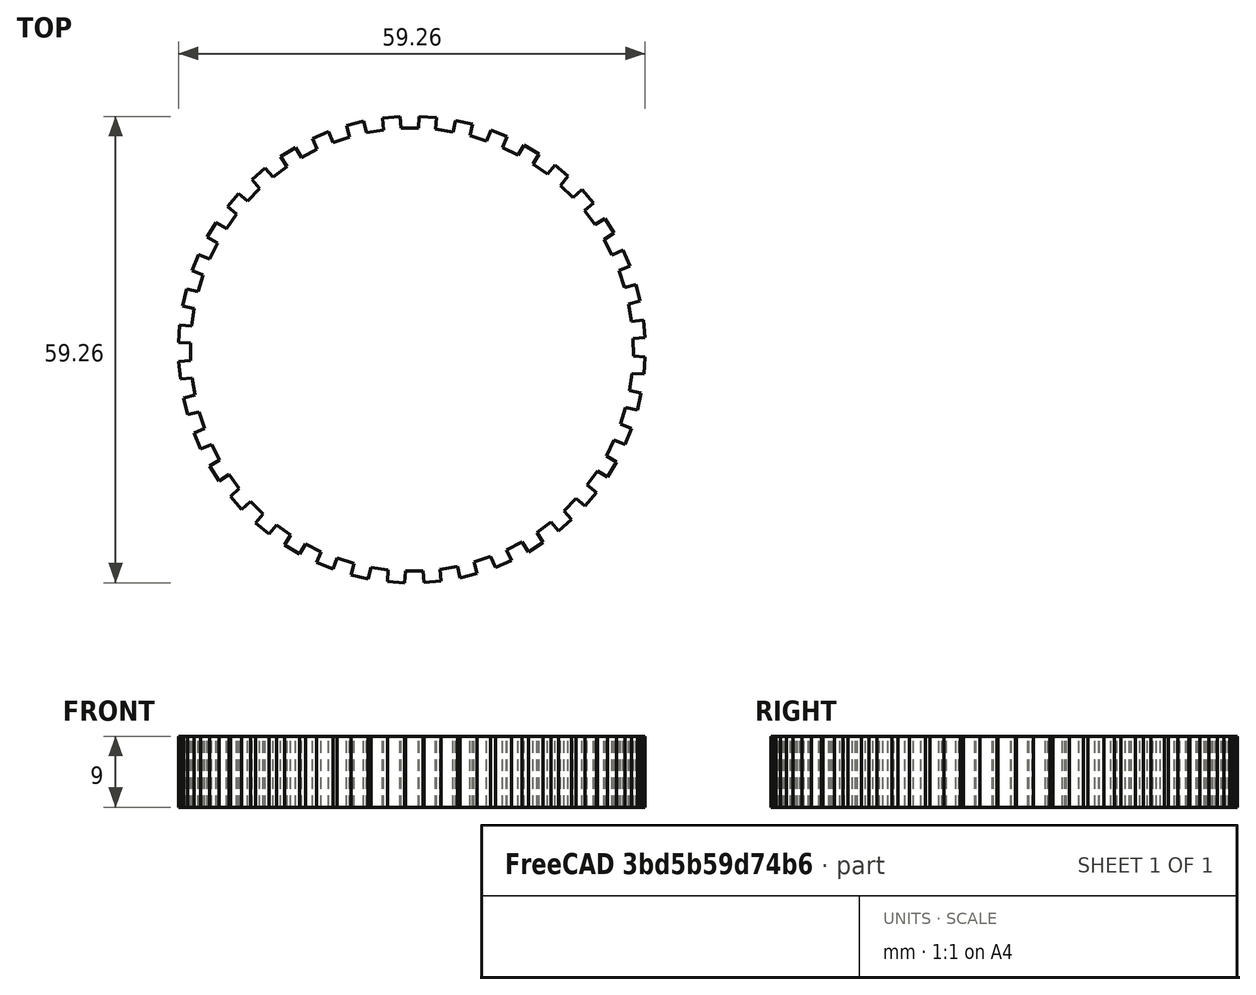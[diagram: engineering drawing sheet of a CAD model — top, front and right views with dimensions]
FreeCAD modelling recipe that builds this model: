
FCSTD DOCUMENT  (FreeCAD 0.19R24276 (Git))
Label: G1
License: All rights reserved
LicenseURL: http://en.wikipedia.org/wiki/All_rights_reserved
objects: Sketcher::SketchObject×1, PartDesign::Pad×1, PartDesign::Body×1
note: 4 computed .brp shape members not serialized (recipe doc carries the construction recipe); baked Part::Feature solids carry a one-line shape summary decoded from their .brp

FEATURE [Sketcher::SketchObject] Sketch
  FullyConstrained = false
  MapMode = 5
  Support = -> [XY_Plane]
  sketch-geometry (281):
    g0: Circle CenterX=0 CenterY=0 CenterZ=0 NormalX=0 NormalY=0 NormalZ=1 AngleXU=0 Radius=28.1239
    g1: LineSegment StartX=-25.682 StartY=11.5162 StartZ=0 EndX=-26.503 EndY=9.47509 EndZ=0
    g2: LineSegment StartX=-26.503 StartY=9.47509 StartZ=0 EndX=-27.8947 EndY=10.0349 EndZ=0
    g3: LineSegment StartX=-27.8947 StartY=10.0349 StartZ=0 EndX=-27.0736 EndY=12.0759 EndZ=0
    g4: LineSegment StartX=-27.0736 StartY=12.0759 StartZ=0 EndX=-25.682 EndY=11.5162 EndZ=0
    g5: GeomPoint X=-26.0925 Y=10.4956 Z=0
    g6: LineSegment StartX=-27.1673 StartY=7.35682 StartZ=0 EndX=-27.659 EndY=5.21245 EndZ=0
    g7: LineSegment StartX=-27.659 StartY=5.21245 StartZ=0 EndX=-29.121 EndY=5.54764 EndZ=0
    g8: LineSegment StartX=-29.121 StartY=5.54764 StartZ=0 EndX=-28.6294 EndY=7.69201 EndZ=0
    g9: LineSegment StartX=-28.6294 StartY=7.69201 StartZ=0 EndX=-27.1673 EndY=7.35682 EndZ=0
    g10: GeomPoint X=-27.4132 Y=6.28463 Z=0
    g11: LineSegment StartX=0 StartY=0 StartZ=0 EndX=-27.4132 EndY=6.28463 EndZ=0
    g12: LineSegment StartX=-26.0925 StartY=10.4956 StartZ=0 EndX=0 EndY=0 EndZ=0
    g13: LineSegment StartX=0 StartY=0 StartZ=0 EndX=-11.0287 EndY=25.8717 EndZ=0
    g14: LineSegment StartX=-5.77874 StartY=27.5462 StartZ=0 EndX=-7.91258 EndY=27.0107 EndZ=0
    g15: LineSegment StartX=-7.91258 StartY=27.0107 StartZ=0 EndX=-8.27769 EndY=28.4656 EndZ=0
    g16: LineSegment StartX=-8.27769 StartY=28.4656 StartZ=0 EndX=-6.14386 EndY=29.0011 EndZ=0
    g17: LineSegment StartX=-6.14386 StartY=29.0011 StartZ=0 EndX=-5.77874 EndY=27.5462 EndZ=0
    g18: GeomPoint X=-6.84566 Y=27.2785 Z=0
    g19: LineSegment StartX=-10.0168 StartY=26.3031 StartZ=0 EndX=-12.0406 EndY=25.4404 EndZ=0
    g20: LineSegment StartX=-12.0406 StartY=25.4404 StartZ=0 EndX=-12.6288 EndY=26.8202 EndZ=0
    g21: LineSegment StartX=-12.6288 StartY=26.8202 StartZ=0 EndX=-10.605 EndY=27.6829 EndZ=0
    g22: LineSegment StartX=-10.605 StartY=27.6829 StartZ=0 EndX=-10.0168 EndY=26.3031 EndZ=0
    g23: GeomPoint X=-11.0287 Y=25.8717 Z=0
    g24: LineSegment StartX=-15.8721 StartY=23.2436 StartZ=0 EndX=-14.0082 EndY=24.4123 EndZ=0
    g25: LineSegment StartX=-14.0082 StartY=24.4123 StartZ=0 EndX=-14.805 EndY=25.6831 EndZ=0
    g26: LineSegment StartX=-14.805 StartY=25.6831 StartZ=0 EndX=-16.6689 EndY=24.5144 EndZ=0
    g27: LineSegment StartX=-16.6689 StartY=24.5144 StartZ=0 EndX=-15.8721 EndY=23.2436 EndZ=0
    g28: GeomPoint X=-14.9401 Y=23.8279 Z=0
    g29: LineSegment StartX=-24.6945 StartY=13.5044 StartZ=0 EndX=-23.5643 EndY=15.3919 EndZ=0
    g30: LineSegment StartX=-23.5643 StartY=15.3919 StartZ=0 EndX=-24.8512 EndY=16.1625 EndZ=0
    g31: LineSegment StartX=-24.8512 StartY=16.1625 StartZ=0 EndX=-25.9814 EndY=14.275 EndZ=0
    g32: LineSegment StartX=-25.9814 StartY=14.275 StartZ=0 EndX=-24.6945 EndY=13.5044 EndZ=0
    g33: GeomPoint X=-24.1294 Y=14.4482 Z=0
    g34: LineSegment StartX=-22.2779 StartY=17.2012 StartZ=0 EndX=-20.8664 EndY=18.8887 EndZ=0
    g35: LineSegment StartX=-20.8664 StartY=18.8887 StartZ=0 EndX=-22.0169 EndY=19.8511 EndZ=0
    g36: LineSegment StartX=-22.0169 StartY=19.8511 StartZ=0 EndX=-23.4285 EndY=18.1637 EndZ=0
    g37: LineSegment StartX=-23.4285 StartY=18.1637 StartZ=0 EndX=-22.2779 EndY=17.2012 EndZ=0
    g38: GeomPoint X=-21.5721 Y=18.045 Z=0
    g39: LineSegment StartX=-17.6546 StartY=21.9204 StartZ=0 EndX=-19.3128 EndY=20.4745 EndZ=0
    g40: LineSegment StartX=-19.3128 StartY=20.4745 StartZ=0 EndX=-20.2986 EndY=21.605 EndZ=0
    g41: LineSegment StartX=-20.2986 StartY=21.605 StartZ=0 EndX=-18.6404 EndY=23.0509 EndZ=0
    g42: LineSegment StartX=-18.6404 StartY=23.0509 StartZ=0 EndX=-17.6546 EndY=21.9204 EndZ=0
    g43: GeomPoint X=-18.4837 Y=21.1974 Z=0
    g44: LineSegment StartX=0 StartY=0 StartZ=0 EndX=-14.9401 EndY=23.8279 EndZ=0
    g45: LineSegment StartX=0 StartY=0 StartZ=0 EndX=-18.4837 EndY=21.1974 EndZ=0
    g46: LineSegment StartX=0 StartY=0 StartZ=0 EndX=-21.5721 EndY=18.045 EndZ=0
    g47: LineSegment StartX=-24.1294 StartY=14.4482 StartZ=0 EndX=0 EndY=0 EndZ=0
    g48: LineSegment StartX=-6.84566 StartY=27.2785 StartZ=0 EndX=0 EndY=0 EndZ=0
    g49: LineSegment StartX=27.9837 StartY=-3.01633 StartZ=0 EndX=28.1338 EndY=-0.821461 EndZ=0
    g50: LineSegment StartX=28.1338 StartY=-0.821461 StartZ=0 EndX=29.6303 EndY=-0.923805 EndZ=0
    g51: LineSegment StartX=29.6303 StartY=-0.923805 StartZ=0 EndX=29.4802 EndY=-3.11868 EndZ=0
    g52: LineSegment StartX=29.4802 StartY=-3.11868 StartZ=0 EndX=27.9837 EndY=-3.01633 EndZ=0
    g53: GeomPoint X=28.0588 Y=-1.9189 Z=0
    g54: LineSegment StartX=28.1111 StartY=1.39842 StartZ=0 EndX=27.916 EndY=3.58975 EndZ=0
    g55: LineSegment StartX=27.916 StartY=3.58975 StartZ=0 EndX=29.4101 EndY=3.72278 EndZ=0
    g56: LineSegment StartX=29.4101 StartY=3.72278 StartZ=0 EndX=29.6052 EndY=1.53144 EndZ=0
    g57: LineSegment StartX=29.6052 StartY=1.53144 StartZ=0 EndX=28.1111 EndY=1.39842 EndZ=0
    g58: GeomPoint X=28.0135 Y=2.49409 Z=0
    g59: LineSegment StartX=27.0107 StartY=7.91258 StartZ=0 EndX=27.5462 EndY=5.77874 EndZ=0
    g60: LineSegment StartX=27.5462 StartY=5.77874 StartZ=0 EndX=29.0011 EndY=6.14386 EndZ=0
    g61: LineSegment StartX=29.0011 StartY=6.14386 StartZ=0 EndX=28.4656 EndY=8.27769 EndZ=0
    g62: LineSegment StartX=28.4656 StartY=8.27769 StartZ=0 EndX=27.0107 EndY=7.91258 EndZ=0
    g63: GeomPoint X=27.2785 Y=6.84566 Z=0
    g64: LineSegment StartX=20.4745 StartY=19.3128 StartZ=0 EndX=21.9204 EndY=17.6546 EndZ=0
    g65: LineSegment StartX=21.9204 StartY=17.6546 StartZ=0 EndX=23.0509 EndY=18.6404 EndZ=0
    g66: LineSegment StartX=23.0509 StartY=18.6404 StartZ=0 EndX=21.605 EndY=20.2986 EndZ=0
    g67: LineSegment StartX=21.605 StartY=20.2986 StartZ=0 EndX=20.4745 EndY=19.3128 EndZ=0
    g68: GeomPoint X=21.1974 Y=18.4837 Z=0
    g69: LineSegment StartX=23.2436 StartY=15.8721 StartZ=0 EndX=24.4123 EndY=14.0082 EndZ=0
    g70: LineSegment StartX=24.4123 StartY=14.0082 StartZ=0 EndX=25.6831 EndY=14.805 EndZ=0
    g71: LineSegment StartX=25.6831 StartY=14.805 StartZ=0 EndX=24.5144 EndY=16.6689 EndZ=0
    g72: LineSegment StartX=24.5144 StartY=16.6689 StartZ=0 EndX=23.2436 EndY=15.8721 EndZ=0
    g73: GeomPoint X=23.8279 Y=14.9401 Z=0
    g74: LineSegment StartX=26.3031 StartY=10.0168 StartZ=0 EndX=25.4404 EndY=12.0406 EndZ=0
    g75: LineSegment StartX=25.4404 StartY=12.0406 StartZ=0 EndX=26.8202 EndY=12.6288 EndZ=0
    g76: LineSegment StartX=26.8202 StartY=12.6288 StartZ=0 EndX=27.6829 EndY=10.605 EndZ=0
    g77: LineSegment StartX=27.6829 StartY=10.605 StartZ=0 EndX=26.3031 EndY=10.0168 EndZ=0
    g78: GeomPoint X=25.8717 Y=11.0287 Z=0
    g79: LineSegment StartX=-3.58975 StartY=27.916 StartZ=0 EndX=-1.39842 EndY=28.1111 EndZ=0
    g80: LineSegment StartX=-1.39842 StartY=28.1111 StartZ=0 EndX=-1.53144 EndY=29.6052 EndZ=0
    g81: LineSegment StartX=-1.53144 StartY=29.6052 StartZ=0 EndX=-3.72278 EndY=29.4101 EndZ=0
    g82: LineSegment StartX=-3.72278 StartY=29.4101 StartZ=0 EndX=-3.58975 EndY=27.916 EndZ=0
    g83: GeomPoint X=-2.49409 Y=28.0135 Z=0
    g84: LineSegment StartX=0.821461 StartY=28.1338 StartZ=0 EndX=3.01633 EndY=27.9837 EndZ=0
    g85: LineSegment StartX=3.01633 StartY=27.9837 StartZ=0 EndX=3.11868 EndY=29.4802 EndZ=0
    g86: LineSegment StartX=3.11868 StartY=29.4802 StartZ=0 EndX=0.923805 EndY=29.6303 EndZ=0
    g87: LineSegment StartX=0.923805 StartY=29.6303 StartZ=0 EndX=0.821461 EndY=28.1338 EndZ=0
    g88: GeomPoint X=1.9189 Y=28.0588 Z=0
    g89: LineSegment StartX=7.35682 StartY=27.1673 StartZ=0 EndX=5.21245 EndY=27.659 EndZ=0
    g90: LineSegment StartX=5.21245 StartY=27.659 StartZ=0 EndX=5.54764 EndY=29.121 EndZ=0
    g91: LineSegment StartX=5.54764 StartY=29.121 StartZ=0 EndX=7.69201 EndY=28.6294 EndZ=0
    g92: LineSegment StartX=7.69201 StartY=28.6294 StartZ=0 EndX=7.35682 EndY=27.1673 EndZ=0
    g93: GeomPoint X=6.28463 Y=27.4132 Z=0
    g94: LineSegment StartX=18.8887 StartY=20.8664 StartZ=0 EndX=17.2012 EndY=22.2779 EndZ=0
    g95: LineSegment StartX=17.2012 StartY=22.2779 StartZ=0 EndX=18.1637 EndY=23.4285 EndZ=0
    g96: LineSegment StartX=18.1637 StartY=23.4285 StartZ=0 EndX=19.8511 EndY=22.0169 EndZ=0
    g97: LineSegment StartX=19.8511 StartY=22.0169 StartZ=0 EndX=18.8887 EndY=20.8664 EndZ=0
    g98: GeomPoint X=18.045 Y=21.5721 Z=0
    g99: LineSegment StartX=15.3919 StartY=23.5643 StartZ=0 EndX=13.5044 EndY=24.6945 EndZ=0
    g100: LineSegment StartX=13.5044 StartY=24.6945 StartZ=0 EndX=14.275 EndY=25.9814 EndZ=0
    g101: LineSegment StartX=14.275 StartY=25.9814 StartZ=0 EndX=16.1625 EndY=24.8512 EndZ=0
    g102: LineSegment StartX=16.1625 StartY=24.8512 StartZ=0 EndX=15.3919 EndY=23.5643 EndZ=0
    g103: GeomPoint X=14.4482 Y=24.1294 Z=0
    g104: LineSegment StartX=9.47509 StartY=26.503 StartZ=0 EndX=11.5162 EndY=25.682 EndZ=0
    g105: LineSegment StartX=11.5162 StartY=25.682 StartZ=0 EndX=12.0759 EndY=27.0736 EndZ=0
    g106: LineSegment StartX=12.0759 StartY=27.0736 StartZ=0 EndX=10.0349 EndY=27.8947 EndZ=0
    g107: LineSegment StartX=10.0349 StartY=27.8947 StartZ=0 EndX=9.47509 EndY=26.503 EndZ=0
    g108: GeomPoint X=10.4956 Y=26.0925 Z=0
    g109: LineSegment StartX=0 StartY=0 StartZ=0 EndX=28.0588 EndY=-1.9189 EndZ=0
    g110: LineSegment StartX=0 StartY=0 StartZ=0 EndX=28.0135 EndY=2.49409 EndZ=0
    g111: LineSegment StartX=0 StartY=0 StartZ=0 EndX=27.2785 EndY=6.84566 EndZ=0
    g112: LineSegment StartX=0 StartY=0 StartZ=0 EndX=23.8279 EndY=14.9401 EndZ=0
    g113: LineSegment StartX=0 StartY=0 StartZ=0 EndX=25.8717 EndY=11.0287 EndZ=0
    g114: LineSegment StartX=21.1974 StartY=18.4837 StartZ=0 EndX=0 EndY=0 EndZ=0
    g115: LineSegment StartX=0 StartY=0 StartZ=0 EndX=10.4956 EndY=26.0925 EndZ=0
    g116: LineSegment StartX=0 StartY=0 StartZ=0 EndX=14.4482 EndY=24.1294 EndZ=0
    g117: LineSegment StartX=18.045 StartY=21.5721 StartZ=0 EndX=0 EndY=0 EndZ=0
    g118: LineSegment StartX=0 StartY=0 StartZ=0 EndX=1.9189 EndY=28.0588 EndZ=0
    g119: LineSegment StartX=0 StartY=0 StartZ=0 EndX=6.28463 EndY=27.4132 EndZ=0
    g120: LineSegment StartX=-2.49409 StartY=28.0135 StartZ=0 EndX=0 EndY=0 EndZ=0
    g121: LineSegment StartX=-27.916 StartY=-3.58975 StartZ=0 EndX=-28.1111 EndY=-1.39842 EndZ=0
    g122: LineSegment StartX=-28.1111 StartY=-1.39842 StartZ=0 EndX=-29.6052 EndY=-1.53144 EndZ=0
    g123: LineSegment StartX=-29.6052 StartY=-1.53144 StartZ=0 EndX=-29.4101 EndY=-3.72278 EndZ=0
    g124: LineSegment StartX=-29.4101 StartY=-3.72278 StartZ=0 EndX=-27.916 EndY=-3.58975 EndZ=0
    g125: GeomPoint X=-28.0135 Y=-2.49409 Z=0
    g126: LineSegment StartX=-28.1338 StartY=0.821461 StartZ=0 EndX=-27.9837 EndY=3.01633 EndZ=0
    g127: LineSegment StartX=-27.9837 StartY=3.01633 StartZ=0 EndX=-29.4802 EndY=3.11868 EndZ=0
    g128: LineSegment StartX=-29.4802 StartY=3.11868 StartZ=0 EndX=-29.6303 EndY=0.923805 EndZ=0
    g129: LineSegment StartX=-29.6303 StartY=0.923805 StartZ=0 EndX=-28.1338 EndY=0.821461 EndZ=0
    g130: GeomPoint X=-28.0588 Y=1.9189 Z=0
    g131: LineSegment StartX=0 StartY=0 StartZ=0 EndX=-28.0588 EndY=1.9189 EndZ=0
    g132: LineSegment StartX=-28.0135 StartY=-2.49409 StartZ=0 EndX=0 EndY=0 EndZ=0
    g133: LineSegment StartX=0 StartY=0 StartZ=0 EndX=-18.045 EndY=-21.5721 EndZ=0
    g134: LineSegment StartX=-13.5044 StartY=-24.6945 StartZ=0 EndX=-15.3919 EndY=-23.5643 EndZ=0
    g135: LineSegment StartX=-15.3919 StartY=-23.5643 StartZ=0 EndX=-16.1625 EndY=-24.8512 EndZ=0
    g136: LineSegment StartX=-16.1625 StartY=-24.8512 StartZ=0 EndX=-14.275 EndY=-25.9814 EndZ=0
    g137: LineSegment StartX=-14.275 StartY=-25.9814 StartZ=0 EndX=-13.5044 EndY=-24.6945 EndZ=0
    g138: GeomPoint X=-14.4482 Y=-24.1294 Z=0
    g139: LineSegment StartX=-17.2012 StartY=-22.2779 StartZ=0 EndX=-18.8887 EndY=-20.8664 EndZ=0
    g140: LineSegment StartX=-18.8887 StartY=-20.8664 StartZ=0 EndX=-19.8511 EndY=-22.0169 EndZ=0
    g141: LineSegment StartX=-19.8511 StartY=-22.0169 StartZ=0 EndX=-18.1637 EndY=-23.4285 EndZ=0
    g142: LineSegment StartX=-18.1637 StartY=-23.4285 StartZ=0 EndX=-17.2012 EndY=-22.2779 EndZ=0
    g143: GeomPoint X=-18.045 Y=-21.5721 Z=0
    g144: LineSegment StartX=-21.9204 StartY=-17.6546 StartZ=0 EndX=-20.4745 EndY=-19.3128 EndZ=0
    g145: LineSegment StartX=-20.4745 StartY=-19.3128 StartZ=0 EndX=-21.605 EndY=-20.2986 EndZ=0
    g146: LineSegment StartX=-21.605 StartY=-20.2986 StartZ=0 EndX=-23.0509 EndY=-18.6404 EndZ=0
    g147: LineSegment StartX=-23.0509 StartY=-18.6404 StartZ=0 EndX=-21.9204 EndY=-17.6546 EndZ=0
    g148: GeomPoint X=-21.1974 Y=-18.4837 Z=0
    g149: LineSegment StartX=-27.5462 StartY=-5.77874 StartZ=0 EndX=-27.0107 EndY=-7.91258 EndZ=0
    g150: LineSegment StartX=-27.0107 StartY=-7.91258 StartZ=0 EndX=-28.4656 EndY=-8.27769 EndZ=0
    g151: LineSegment StartX=-28.4656 StartY=-8.27769 StartZ=0 EndX=-29.0011 EndY=-6.14386 EndZ=0
    g152: LineSegment StartX=-29.0011 StartY=-6.14386 StartZ=0 EndX=-27.5462 EndY=-5.77874 EndZ=0
    g153: GeomPoint X=-27.2785 Y=-6.84566 Z=0
    g154: LineSegment StartX=-26.3031 StartY=-10.0168 StartZ=0 EndX=-25.4404 EndY=-12.0406 EndZ=0
    g155: LineSegment StartX=-25.4404 StartY=-12.0406 StartZ=0 EndX=-26.8202 EndY=-12.6288 EndZ=0
    g156: LineSegment StartX=-26.8202 StartY=-12.6288 StartZ=0 EndX=-27.6829 EndY=-10.605 EndZ=0
    g157: LineSegment StartX=-27.6829 StartY=-10.605 StartZ=0 EndX=-26.3031 EndY=-10.0168 EndZ=0
    g158: GeomPoint X=-25.8717 Y=-11.0287 Z=0
    g159: LineSegment StartX=-23.2436 StartY=-15.8721 StartZ=0 EndX=-24.4123 EndY=-14.0082 EndZ=0
    g160: LineSegment StartX=-24.4123 StartY=-14.0082 StartZ=0 EndX=-25.6831 EndY=-14.805 EndZ=0
    g161: LineSegment StartX=-25.6831 StartY=-14.805 StartZ=0 EndX=-24.5144 EndY=-16.6689 EndZ=0
    g162: LineSegment StartX=-24.5144 StartY=-16.6689 StartZ=0 EndX=-23.2436 EndY=-15.8721 EndZ=0
    g163: GeomPoint X=-23.8279 Y=-14.9401 Z=0
    g164: LineSegment StartX=0 StartY=0 StartZ=0 EndX=-21.1974 EndY=-18.4837 EndZ=0
    g165: LineSegment StartX=0 StartY=0 StartZ=0 EndX=-23.8279 EndY=-14.9401 EndZ=0
    g166: LineSegment StartX=0 StartY=0 StartZ=0 EndX=-25.8717 EndY=-11.0287 EndZ=0
    g167: LineSegment StartX=-27.2785 StartY=-6.84566 StartZ=0 EndX=0 EndY=0 EndZ=0
    g168: LineSegment StartX=-14.4482 StartY=-24.1294 StartZ=0 EndX=1.8e-15 EndY=0 EndZ=0
    g169: LineSegment StartX=27.659 StartY=-5.21245 StartZ=0 EndX=27.1673 EndY=-7.35682 EndZ=0
    g170: LineSegment StartX=27.1673 StartY=-7.35682 StartZ=0 EndX=28.6294 EndY=-7.69201 EndZ=0
    g171: LineSegment StartX=28.6294 StartY=-7.69201 StartZ=0 EndX=29.121 EndY=-5.54764 EndZ=0
    g172: LineSegment StartX=29.121 StartY=-5.54764 StartZ=0 EndX=27.659 EndY=-5.21245 EndZ=0
    g173: GeomPoint X=27.4132 Y=-6.28463 Z=0
    g174: LineSegment StartX=26.503 StartY=-9.47509 StartZ=0 EndX=25.682 EndY=-11.5162 EndZ=0
    g175: LineSegment StartX=25.682 StartY=-11.5162 StartZ=0 EndX=27.0736 EndY=-12.0759 EndZ=0
    g176: LineSegment StartX=27.0736 StartY=-12.0759 StartZ=0 EndX=27.8947 EndY=-10.0349 EndZ=0
    g177: LineSegment StartX=27.8947 StartY=-10.0349 StartZ=0 EndX=26.503 EndY=-9.47509 EndZ=0
    g178: GeomPoint X=26.0925 Y=-10.4956 Z=0
    g179: LineSegment StartX=23.5643 StartY=-15.3919 StartZ=0 EndX=24.6945 EndY=-13.5044 EndZ=0
    g180: LineSegment StartX=24.6945 StartY=-13.5044 StartZ=0 EndX=25.9814 EndY=-14.275 EndZ=0
    g181: LineSegment StartX=25.9814 StartY=-14.275 StartZ=0 EndX=24.8512 EndY=-16.1625 EndZ=0
    g182: LineSegment StartX=24.8512 StartY=-16.1625 StartZ=0 EndX=23.5643 EndY=-15.3919 EndZ=0
    g183: GeomPoint X=24.1294 Y=-14.4482 Z=0
    g184: LineSegment StartX=14.0082 StartY=-24.4123 StartZ=0 EndX=15.8721 EndY=-23.2436 EndZ=0
    g185: LineSegment StartX=15.8721 StartY=-23.2436 StartZ=0 EndX=16.6689 EndY=-24.5144 EndZ=0
    g186: LineSegment StartX=16.6689 StartY=-24.5144 StartZ=0 EndX=14.805 EndY=-25.6831 EndZ=0
    g187: LineSegment StartX=14.805 StartY=-25.6831 StartZ=0 EndX=14.0082 EndY=-24.4123 EndZ=0
    g188: GeomPoint X=14.9401 Y=-23.8279 Z=0
    g189: LineSegment StartX=17.6546 StartY=-21.9204 StartZ=0 EndX=19.3128 EndY=-20.4745 EndZ=0
    g190: LineSegment StartX=19.3128 StartY=-20.4745 StartZ=0 EndX=20.2986 EndY=-21.605 EndZ=0
    g191: LineSegment StartX=20.2986 StartY=-21.605 StartZ=0 EndX=18.6404 EndY=-23.0509 EndZ=0
    g192: LineSegment StartX=18.6404 StartY=-23.0509 StartZ=0 EndX=17.6546 EndY=-21.9204 EndZ=0
    g193: GeomPoint X=18.4837 Y=-21.1974 Z=0
    g194: LineSegment StartX=22.2779 StartY=-17.2012 StartZ=0 EndX=20.8664 EndY=-18.8887 EndZ=0
    g195: LineSegment StartX=20.8664 StartY=-18.8887 StartZ=0 EndX=22.0169 EndY=-19.8511 EndZ=0
    g196: LineSegment StartX=22.0169 StartY=-19.8511 StartZ=0 EndX=23.4285 EndY=-18.1637 EndZ=0
    g197: LineSegment StartX=23.4285 StartY=-18.1637 StartZ=0 EndX=22.2779 EndY=-17.2012 EndZ=0
    g198: GeomPoint X=21.5721 Y=-18.045 Z=0
    g199: LineSegment StartX=-11.5162 StartY=-25.682 StartZ=0 EndX=-9.47509 EndY=-26.503 EndZ=0
    g200: LineSegment StartX=-9.47509 StartY=-26.503 StartZ=0 EndX=-10.0349 EndY=-27.8947 EndZ=0
    g201: LineSegment StartX=-10.0349 StartY=-27.8947 StartZ=0 EndX=-12.0759 EndY=-27.0736 EndZ=0
    g202: LineSegment StartX=-12.0759 StartY=-27.0736 StartZ=0 EndX=-11.5162 EndY=-25.682 EndZ=0
    g203: GeomPoint X=-10.4956 Y=-26.0925 Z=0
    g204: LineSegment StartX=-7.35682 StartY=-27.1673 StartZ=0 EndX=-5.21245 EndY=-27.659 EndZ=0
    g205: LineSegment StartX=-5.21245 StartY=-27.659 StartZ=0 EndX=-5.54764 EndY=-29.121 EndZ=0
    g206: LineSegment StartX=-5.54764 StartY=-29.121 StartZ=0 EndX=-7.69201 EndY=-28.6294 EndZ=0
    g207: LineSegment StartX=-7.69201 StartY=-28.6294 StartZ=0 EndX=-7.35682 EndY=-27.1673 EndZ=0
    g208: GeomPoint X=-6.28463 Y=-27.4132 Z=0
    g209: LineSegment StartX=-0.821461 StartY=-28.1338 StartZ=0 EndX=-3.01633 EndY=-27.9837 EndZ=0
    g210: LineSegment StartX=-3.01633 StartY=-27.9837 StartZ=0 EndX=-3.11868 EndY=-29.4802 EndZ=0
    g211: LineSegment StartX=-3.11868 StartY=-29.4802 StartZ=0 EndX=-0.923805 EndY=-29.6303 EndZ=0
    g212: LineSegment StartX=-0.923805 StartY=-29.6303 StartZ=0 EndX=-0.821461 EndY=-28.1338 EndZ=0
    g213: GeomPoint X=-1.9189 Y=-28.0588 Z=0
    g214: LineSegment StartX=12.0406 StartY=-25.4404 StartZ=0 EndX=10.0168 EndY=-26.3031 EndZ=0
    g215: LineSegment StartX=10.0168 StartY=-26.3031 StartZ=0 EndX=10.605 EndY=-27.6829 EndZ=0
    g216: LineSegment StartX=10.605 StartY=-27.6829 StartZ=0 EndX=12.6288 EndY=-26.8202 EndZ=0
    g217: LineSegment StartX=12.6288 StartY=-26.8202 StartZ=0 EndX=12.0406 EndY=-25.4404 EndZ=0
    g218: GeomPoint X=11.0287 Y=-25.8717 Z=0
    g219: LineSegment StartX=7.91258 StartY=-27.0107 StartZ=0 EndX=5.77874 EndY=-27.5462 EndZ=0
    g220: LineSegment StartX=5.77874 StartY=-27.5462 StartZ=0 EndX=6.14386 EndY=-29.0011 EndZ=0
    g221: LineSegment StartX=6.14386 StartY=-29.0011 StartZ=0 EndX=8.27769 EndY=-28.4656 EndZ=0
    g222: LineSegment StartX=8.27769 StartY=-28.4656 StartZ=0 EndX=7.91258 EndY=-27.0107 EndZ=0
    g223: GeomPoint X=6.84566 Y=-27.2785 Z=0
    g224: LineSegment StartX=1.39842 StartY=-28.1111 StartZ=0 EndX=3.58975 EndY=-27.916 EndZ=0
    g225: LineSegment StartX=3.58975 StartY=-27.916 StartZ=0 EndX=3.72278 EndY=-29.4101 EndZ=0
    g226: LineSegment StartX=3.72278 StartY=-29.4101 StartZ=0 EndX=1.53144 EndY=-29.6052 EndZ=0
    g227: LineSegment StartX=1.53144 StartY=-29.6052 StartZ=0 EndX=1.39842 EndY=-28.1111 EndZ=0
    g228: GeomPoint X=2.49409 Y=-28.0135 Z=0
    g229: LineSegment StartX=0 StartY=0 StartZ=0 EndX=27.4132 EndY=-6.28463 EndZ=0
    g230: LineSegment StartX=0 StartY=0 StartZ=0 EndX=26.0925 EndY=-10.4956 EndZ=0
    g231: LineSegment StartX=0 StartY=0 StartZ=0 EndX=24.1294 EndY=-14.4482 EndZ=0
    g232: LineSegment StartX=0 StartY=0 StartZ=0 EndX=18.4837 EndY=-21.1974 EndZ=0
    g233: LineSegment StartX=0 StartY=0 StartZ=0 EndX=21.5721 EndY=-18.045 EndZ=0
    g234: LineSegment StartX=14.9401 StartY=-23.8279 StartZ=0 EndX=0 EndY=0 EndZ=0
    g235: LineSegment StartX=0 StartY=0 StartZ=0 EndX=2.49409 EndY=-28.0135 EndZ=0
    g236: LineSegment StartX=0 StartY=0 StartZ=0 EndX=6.84566 EndY=-27.2785 EndZ=0
    g237: LineSegment StartX=11.0287 StartY=-25.8717 StartZ=0 EndX=0 EndY=0 EndZ=0
    g238: LineSegment StartX=0 StartY=0 StartZ=0 EndX=-6.28463 EndY=-27.4132 EndZ=0
    g239: LineSegment StartX=0 StartY=0 StartZ=0 EndX=-1.9189 EndY=-28.0588 EndZ=0
    g240: LineSegment StartX=-10.4956 StartY=-26.0925 StartZ=0 EndX=0 EndY=0 EndZ=0
    g241: LineSegment StartX=11.5162 StartY=25.682 StartZ=0 EndX=13.5044 EndY=24.6945 EndZ=0
    g242: LineSegment StartX=15.3919 StartY=23.5643 StartZ=0 EndX=17.2012 EndY=22.2779 EndZ=0
    g243: LineSegment StartX=18.8887 StartY=20.8664 StartZ=0 EndX=20.4745 EndY=19.3128 EndZ=0
    g244: LineSegment StartX=21.9204 StartY=17.6546 StartZ=0 EndX=23.2436 EndY=15.8721 EndZ=0
    g245: LineSegment StartX=24.4123 StartY=14.0082 StartZ=0 EndX=25.4404 EndY=12.0406 EndZ=0
    g246: LineSegment StartX=26.3031 StartY=10.0168 StartZ=0 EndX=27.0107 EndY=7.91258 EndZ=0
    g247: LineSegment StartX=27.5462 StartY=5.77874 StartZ=0 EndX=27.916 EndY=3.58975 EndZ=0
    g248: LineSegment StartX=28.1111 StartY=1.39842 StartZ=0 EndX=28.1338 EndY=-0.821461 EndZ=0
    g249: LineSegment StartX=27.9837 StartY=-3.01633 StartZ=0 EndX=27.659 EndY=-5.21245 EndZ=0
    g250: LineSegment StartX=27.1673 StartY=-7.35682 StartZ=0 EndX=26.503 EndY=-9.47509 EndZ=0
    g251: LineSegment StartX=25.682 StartY=-11.5162 StartZ=0 EndX=24.6945 EndY=-13.5044 EndZ=0
    g252: LineSegment StartX=23.5643 StartY=-15.3919 StartZ=0 EndX=22.2779 EndY=-17.2012 EndZ=0
    g253: LineSegment StartX=20.8664 StartY=-18.8887 StartZ=0 EndX=19.3128 EndY=-20.4745 EndZ=0
    g254: LineSegment StartX=17.6546 StartY=-21.9204 StartZ=0 EndX=15.8721 EndY=-23.2436 EndZ=0
    g255: LineSegment StartX=14.0082 StartY=-24.4123 StartZ=0 EndX=12.0406 EndY=-25.4404 EndZ=0
    g256: LineSegment StartX=10.0168 StartY=-26.3031 StartZ=0 EndX=7.91258 EndY=-27.0107 EndZ=0
    g257: LineSegment StartX=5.77874 StartY=-27.5462 StartZ=0 EndX=3.58975 EndY=-27.916 EndZ=0
    g258: LineSegment StartX=1.39842 StartY=-28.1111 StartZ=0 EndX=-0.821461 EndY=-28.1338 EndZ=0
    g259: LineSegment StartX=-3.01633 StartY=-27.9837 StartZ=0 EndX=-5.21245 EndY=-27.659 EndZ=0
    g260: LineSegment StartX=-7.35682 StartY=-27.1673 StartZ=0 EndX=-9.47509 EndY=-26.503 EndZ=0
    g261: LineSegment StartX=-11.5162 StartY=-25.682 StartZ=0 EndX=-13.5044 EndY=-24.6945 EndZ=0
    g262: LineSegment StartX=-15.3919 StartY=-23.5643 StartZ=0 EndX=-17.2012 EndY=-22.2779 EndZ=0
    g263: LineSegment StartX=-18.8887 StartY=-20.8664 StartZ=0 EndX=-20.4745 EndY=-19.3128 EndZ=0
    g264: LineSegment StartX=-21.9204 StartY=-17.6546 StartZ=0 EndX=-23.2436 EndY=-15.8721 EndZ=0
    g265: LineSegment StartX=-24.4123 StartY=-14.0082 StartZ=0 EndX=-25.4404 EndY=-12.0406 EndZ=0
    g266: LineSegment StartX=-26.3031 StartY=-10.0168 StartZ=0 EndX=-27.0107 EndY=-7.91258 EndZ=0
    g267: LineSegment StartX=-27.5462 StartY=-5.77874 StartZ=0 EndX=-27.916 EndY=-3.58975 EndZ=0
    g268: LineSegment StartX=-28.1111 StartY=-1.39842 StartZ=0 EndX=-28.1338 EndY=0.821461 EndZ=0
    g269: LineSegment StartX=-27.9837 StartY=3.01633 StartZ=0 EndX=-27.659 EndY=5.21245 EndZ=0
    g270: LineSegment StartX=-27.1673 StartY=7.35682 StartZ=0 EndX=-26.503 EndY=9.47509 EndZ=0
    g271: LineSegment StartX=-25.682 StartY=11.5162 StartZ=0 EndX=-24.6945 EndY=13.5044 EndZ=0
    g272: LineSegment StartX=-23.5643 StartY=15.3919 StartZ=0 EndX=-22.2779 EndY=17.2012 EndZ=0
    g273: LineSegment StartX=-20.8664 StartY=18.8887 StartZ=0 EndX=-19.3128 EndY=20.4745 EndZ=0
    g274: LineSegment StartX=-17.6546 StartY=21.9204 StartZ=0 EndX=-15.8721 EndY=23.2436 EndZ=0
    g275: LineSegment StartX=-10.0168 StartY=26.3031 StartZ=0 EndX=-7.91258 EndY=27.0107 EndZ=0
    g276: LineSegment StartX=-5.77874 StartY=27.5462 StartZ=0 EndX=-3.58975 EndY=27.916 EndZ=0
    g277: LineSegment StartX=-1.39842 StartY=28.1111 StartZ=0 EndX=0.821461 EndY=28.1338 EndZ=0
    g278: LineSegment StartX=3.01633 StartY=27.9837 StartZ=0 EndX=5.21245 EndY=27.659 EndZ=0
    g279: LineSegment StartX=7.35682 StartY=27.1673 StartZ=0 EndX=9.47509 EndY=26.503 EndZ=0
    g280: LineSegment StartX=-14.0082 StartY=24.4123 StartZ=0 EndX=-12.0406 EndY=25.4404 EndZ=0
  constraints (721):
    c: Coincident(g0,g-1)
    c: Coincident(g2,g1)
    c: Coincident(g3,g2)
    c: Coincident(g4,g3)
    c: Coincident(g4,g1)
    c: Equal(g1,g3)
    c: Parallel(g2,g4)
    c: Perpendicular(g2,g1)
    c: PointOnObject(g5,g1)
    c: Distance(g5,g1) = 1.1
    c: Distance(g1,g1) = 2.2
    c: Distance(g1,g2) = 1.5
    c: Coincident(g7,g6)
    c: Coincident(g8,g7)
    c: Coincident(g9,g8)
    c: Coincident(g9,g6)
    c: Equal(g6,g8)
    c: Parallel(g7,g9)
    c: Perpendicular(g7,g6)
    c: PointOnObject(g10,g6)
    c: Distance(g10,g6) = 1.1
    c: Equal(g1,g6) = 2.2
    c: Distance(g6,g7) = 1.5
    c: Coincident(g10,g11)
    c: Perpendicular(g11,g6)
    c: Distance(g1,g6) = 2.22
    c: Coincident(g11,g0)
    c: Coincident(g12,g5)
    c: Coincident(g12,g0)
    c: Perpendicular(g12,g1)
    c: Equal(g11,g12)
    c: Coincident(g15,g14)
    c: Coincident(g16,g15)
    c: Coincident(g17,g16)
    c: Coincident(g17,g14)
    c: Equal(g14,g16)
    c: Parallel(g15,g17)
    c: Perpendicular(g15,g14)
    c: PointOnObject(g18,g14)
    c: Distance(g18,g14) = 1.1
    c: Distance(g14,g14) = 2.2
    c: Distance(g14,g15) = 1.5
    c: Coincident(g20,g19)
    c: Coincident(g21,g20)
    c: Coincident(g22,g21)
    c: Coincident(g22,g19)
    c: Equal(g19,g21)
    c: Parallel(g20,g22)
    c: Perpendicular(g20,g19)
    c: PointOnObject(g23,g19)
    c: Distance(g23,g19) = 1.1
    c: Equal(g14,g19) = 2.2
    c: Distance(g19,g20) = 1.5
    c: Coincident(g23,g13)
    c: Perpendicular(g13,g19)
    c: Distance(g14,g19) = 2.22
    c: Coincident(g25,g24)
    c: Coincident(g26,g25)
    c: Coincident(g27,g26)
    c: Coincident(g27,g24)
    c: Equal(g24,g26)
    c: Parallel(g25,g27)
    c: Perpendicular(g25,g24)
    c: PointOnObject(g28,g24)
    c: Distance(g28,g24) = 1.1
    c: Distance(g24,g24) = 2.2
    c: Distance(g24,g25) = 1.5
    c: Coincident(g28,g44)
    c: Perpendicular(g44,g24)
    c: Coincident(g30,g29)
    c: Coincident(g31,g30)
    c: Coincident(g32,g31)
    c: Coincident(g32,g29)
    c: Equal(g29,g31)
    c: Parallel(g30,g32)
    c: Perpendicular(g30,g29)
    c: PointOnObject(g33,g29)
    c: Distance(g33,g29) = 1.1
    c: Distance(g29,g29) = 2.2
    c: Distance(g29,g30) = 1.5
    c: Coincident(g35,g34)
    c: Coincident(g36,g35)
    c: Coincident(g37,g36)
    c: Coincident(g37,g34)
    c: Equal(g34,g36)
    c: Parallel(g35,g37)
    c: Perpendicular(g35,g34)
    c: PointOnObject(g38,g34)
    c: Distance(g38,g34) = 1.1
    c: Equal(g29,g34) = 2.2
    c: Distance(g34,g35) = 1.5
    c: Coincident(g38,g46)
    c: Perpendicular(g46,g34)
    c: Distance(g29,g34) = 2.22
    c: Coincident(g40,g39)
    c: Coincident(g41,g40)
    c: Coincident(g42,g41)
    c: Coincident(g42,g39)
    c: Equal(g39,g41)
    c: Parallel(g40,g42)
    c: Perpendicular(g40,g39)
    c: PointOnObject(g43,g39)
    c: Distance(g43,g39) = 1.1
    c: Distance(g39,g39) = 2.2
    c: Distance(g39,g40) = 1.5
    c: Coincident(g43,g45)
    c: Perpendicular(g45,g39)
    c: Angle(g45,g44) = -0.15708
    c: Angle(g46,g45) = -0.15708
    c: Angle(g44,g13) = -0.15708
    c: Equal(g13,g44)
    c: Equal(g44,g45)
    c: Equal(g45,g46)
    c: Coincident(g47,g33)
    c: Perpendicular(g47,g29)
    c: Equal(g46,g47)
    c: Angle(g47,g12) = 0.15708
    c: Coincident(g47,g0)
    c: Coincident(g46,g0)
    c: Coincident(g44,g0)
    c: Coincident(g45,g0)
    c: Coincident(g13,g0)
    c: Equal(g12,g47)
    c: Coincident(g48,g18)
    c: Coincident(g48,g0)
    c: Equal(g13,g48)
    c: Perpendicular(g48,g14)
    c: Coincident(g50,g49)
    c: Coincident(g51,g50)
    c: Coincident(g52,g51)
    c: Coincident(g52,g49)
    c: Equal(g49,g51)
    c: Parallel(g50,g52)
    c: Perpendicular(g50,g49)
    c: PointOnObject(g53,g49)
    c: Distance(g53,g49) = 1.1
    c: Distance(g49,g49) = 2.2
    c: Distance(g49,g50) = 1.5
    c: Coincident(g53,g109)
    c: Perpendicular(g109,g49)
    c: Angle(g110,g109) = -0.15708
    c: Coincident(g55,g54)
    c: Coincident(g56,g55)
    c: Coincident(g57,g56)
    c: Coincident(g57,g54)
    c: Equal(g54,g56)
    c: Parallel(g55,g57)
    c: Perpendicular(g55,g54)
    c: PointOnObject(g58,g54)
    c: Distance(g58,g54) = 1.1
    c: Equal(g49,g54) = 2.2
    c: Distance(g54,g55) = 1.5
    c: Coincident(g58,g110)
    c: Perpendicular(g110,g54)
    c: Distance(g49,g54) = 2.22
    c: Coincident(g60,g59)
    c: Coincident(g61,g60)
    c: Coincident(g62,g61)
    c: Coincident(g62,g59)
    c: Equal(g59,g61)
    c: Parallel(g60,g62)
    c: Perpendicular(g60,g59)
    c: PointOnObject(g63,g59)
    c: Distance(g63,g59) = 1.1
    c: Distance(g59,g59) = 2.2
    c: Distance(g59,g60) = 1.5
    c: Coincident(g63,g111)
    c: Perpendicular(g111,g59)
    c: Coincident(g65,g64)
    c: Coincident(g66,g65)
    c: Coincident(g67,g66)
    c: Coincident(g67,g64)
    c: Equal(g64,g66)
    c: Parallel(g65,g67)
    c: Perpendicular(g65,g64)
    c: PointOnObject(g68,g64)
    c: Distance(g68,g64) = 1.1
    c: Distance(g64,g64) = 2.2
    c: Distance(g64,g65) = 1.5
    c: Coincident(g70,g69)
    c: Coincident(g71,g70)
    c: Coincident(g72,g71)
    c: Coincident(g72,g69)
    c: Equal(g69,g71)
    c: Parallel(g70,g72)
    c: Perpendicular(g70,g69)
    c: PointOnObject(g73,g69)
    c: Distance(g73,g69) = 1.1
    c: Equal(g64,g69) = 2.2
    c: Distance(g69,g70) = 1.5
    c: Coincident(g73,g112)
    c: Perpendicular(g112,g69)
    c: Distance(g64,g69) = 2.22
    c: Coincident(g75,g74)
    c: Coincident(g76,g75)
    c: Coincident(g77,g76)
    c: Coincident(g77,g74)
    c: Equal(g74,g76)
    c: Parallel(g75,g77)
    c: Perpendicular(g75,g74)
    c: PointOnObject(g78,g74)
    c: Distance(g78,g74) = 1.1
    c: Distance(g74,g74) = 2.2
    c: Distance(g74,g75) = 1.5
    c: Coincident(g78,g113)
    c: Perpendicular(g113,g74)
    c: Angle(g113,g111) = -0.15708
    c: Angle(g112,g113) = -0.15708
    c: Angle(g111,g110) = -0.15708
    c: Equal(g110,g111)
    c: Equal(g111,g113)
    c: Equal(g113,g112)
    c: Coincident(g114,g68)
    c: Perpendicular(g114,g64)
    c: Equal(g112,g114)
    c: Coincident(g80,g79)
    c: Coincident(g81,g80)
    c: Coincident(g82,g81)
    c: Coincident(g82,g79)
    c: Equal(g79,g81)
    c: Parallel(g80,g82)
    c: Perpendicular(g80,g79)
    c: PointOnObject(g83,g79)
    c: Distance(g83,g79) = 1.1
    c: Distance(g79,g79) = 2.2
    c: Distance(g79,g80) = 1.5
    c: Coincident(g85,g84)
    c: Coincident(g86,g85)
    c: Coincident(g87,g86)
    c: Coincident(g87,g84)
    c: Equal(g84,g86)
    c: Parallel(g85,g87)
    c: Perpendicular(g85,g84)
    c: PointOnObject(g88,g84)
    c: Distance(g88,g84) = 1.1
    c: Equal(g79,g84) = 2.2
    c: Distance(g84,g85) = 1.5
    c: Coincident(g88,g118)
    c: Perpendicular(g118,g84)
    c: Distance(g79,g84) = 2.22
    c: Coincident(g90,g89)
    c: Coincident(g91,g90)
    c: Coincident(g92,g91)
    c: Coincident(g92,g89)
    c: Equal(g89,g91)
    c: Parallel(g90,g92)
    c: Perpendicular(g90,g89)
    c: PointOnObject(g93,g89)
    c: Distance(g93,g89) = 1.1
    c: Distance(g89,g89) = 2.2
    c: Distance(g89,g90) = 1.5
    c: Coincident(g93,g119)
    c: Perpendicular(g119,g89)
    c: Coincident(g95,g94)
    c: Coincident(g96,g95)
    c: Coincident(g97,g96)
    c: Coincident(g97,g94)
    c: Equal(g94,g96)
    c: Parallel(g95,g97)
    c: Perpendicular(g95,g94)
    c: PointOnObject(g98,g94)
    c: Distance(g98,g94) = 1.1
    c: Distance(g94,g94) = 2.2
    c: Distance(g94,g95) = 1.5
    c: Coincident(g100,g99)
    c: Coincident(g101,g100)
    c: Coincident(g102,g101)
    c: Coincident(g102,g99)
    c: Equal(g99,g101)
    c: Parallel(g100,g102)
    c: Perpendicular(g100,g99)
    c: PointOnObject(g103,g99)
    c: Distance(g103,g99) = 1.1
    c: Equal(g94,g99) = 2.2
    c: Distance(g99,g100) = 1.5
    c: Coincident(g103,g116)
    c: Perpendicular(g116,g99)
    c: Coincident(g105,g104)
    c: Coincident(g106,g105)
    c: Coincident(g107,g106)
    c: Coincident(g107,g104)
    c: Equal(g104,g106)
    c: Parallel(g105,g107)
    c: Perpendicular(g105,g104)
    c: PointOnObject(g108,g104)
    c: Distance(g108,g104) = 1.1
    c: Distance(g104,g104) = 2.2
    c: Distance(g104,g105) = 1.5
    c: Coincident(g108,g115)
    c: Perpendicular(g115,g104)
    c: Angle(g115,g119) = 0.15708
    c: Angle(g116,g115) = 0.15708
    c: Angle(g119,g118) = 0.15708
    c: Equal(g118,g119)
    c: Equal(g119,g115)
    c: Equal(g115,g116)
    c: Coincident(g117,g98)
    c: Perpendicular(g117,g94)
    c: Equal(g116,g117)
    c: Angle(g117,g114) = -0.15708
    c: Equal(g114,g117)
    c: Coincident(g120,g83)
    c: Equal(g118,g120)
    c: Perpendicular(g120,g79)
    c: Angle(g120,g48) = 0.15708
    c: Coincident(g118,g0)
    c: Coincident(g120,g0)
    c: Coincident(g117,g0)
    c: Coincident(g111,g0)
    c: Coincident(g112,g0)
    c: Coincident(g113,g0)
    c: Coincident(g110,g0)
    c: Coincident(g109,g0)
    c: Coincident(g114,g119)
    c: Coincident(g114,g115)
    c: Coincident(g114,g116)
    c: Coincident(g114,g0)
    c: Equal(g48,g120)
    c: Equal(g109,g110)
    c: Coincident(g122,g121)
    c: Coincident(g123,g122)
    c: Coincident(g124,g123)
    c: Coincident(g124,g121)
    c: Equal(g121,g123)
    c: Parallel(g122,g124)
    c: Perpendicular(g122,g121)
    c: PointOnObject(g125,g121)
    c: Distance(g125,g121) = 1.1
    c: Distance(g121,g121) = 2.2
    c: Distance(g121,g122) = 1.5
    c: Coincident(g127,g126)
    c: Coincident(g128,g127)
    c: Coincident(g129,g128)
    c: Coincident(g129,g126)
    c: Equal(g126,g128)
    c: Parallel(g127,g129)
    c: Perpendicular(g127,g126)
    c: PointOnObject(g130,g126)
    c: Distance(g130,g126) = 1.1
    c: Equal(g121,g126) = 2.2
    c: Distance(g126,g127) = 1.5
    c: Coincident(g130,g131)
    c: Perpendicular(g131,g126)
    c: Distance(g121,g126) = 2.22
    c: Coincident(g132,g125)
    c: Perpendicular(g132,g121)
    c: Equal(g131,g132)
    c: Coincident(g135,g134)
    c: Coincident(g136,g135)
    c: Coincident(g137,g136)
    c: Coincident(g137,g134)
    c: Equal(g134,g136)
    c: Parallel(g135,g137)
    c: Perpendicular(g135,g134)
    c: PointOnObject(g138,g134)
    c: Distance(g138,g134) = 1.1
    c: Distance(g134,g134) = 2.2
    c: Distance(g134,g135) = 1.5
    c: Coincident(g140,g139)
    c: Coincident(g141,g140)
    c: Coincident(g142,g141)
    c: Coincident(g142,g139)
    c: Equal(g139,g141)
    c: Parallel(g140,g142)
    c: Perpendicular(g140,g139)
    c: PointOnObject(g143,g139)
    c: Distance(g143,g139) = 1.1
    c: Equal(g134,g139) = 2.2
    c: Distance(g139,g140) = 1.5
    c: Coincident(g143,g133)
    c: Perpendicular(g133,g139)
    c: Distance(g134,g139) = 2.22
    c: Coincident(g145,g144)
    c: Coincident(g146,g145)
    c: Coincident(g147,g146)
    c: Coincident(g147,g144)
    c: Equal(g144,g146)
    c: Parallel(g145,g147)
    c: Perpendicular(g145,g144)
    c: PointOnObject(g148,g144)
    c: Distance(g148,g144) = 1.1
    c: Distance(g144,g144) = 2.2
    c: Distance(g144,g145) = 1.5
    c: Coincident(g148,g164)
    c: Perpendicular(g164,g144)
    c: Coincident(g150,g149)
    c: Coincident(g151,g150)
    c: Coincident(g152,g151)
    c: Coincident(g152,g149)
    c: Equal(g149,g151)
    c: Parallel(g150,g152)
    c: Perpendicular(g150,g149)
    c: PointOnObject(g153,g149)
    c: Distance(g153,g149) = 1.1
    c: Distance(g149,g149) = 2.2
    c: Distance(g149,g150) = 1.5
    c: Coincident(g155,g154)
    c: Coincident(g156,g155)
    c: Coincident(g157,g156)
    c: Coincident(g157,g154)
    c: Equal(g154,g156)
    c: Parallel(g155,g157)
    c: Perpendicular(g155,g154)
    c: PointOnObject(g158,g154)
    c: Distance(g158,g154) = 1.1
    c: Equal(g149,g154) = 2.2
    c: Distance(g154,g155) = 1.5
    c: Coincident(g158,g166)
    c: Perpendicular(g166,g154)
    c: Distance(g149,g154) = 2.22
    c: Coincident(g160,g159)
    c: Coincident(g161,g160)
    c: Coincident(g162,g161)
    c: Coincident(g162,g159)
    c: Equal(g159,g161)
    c: Parallel(g160,g162)
    c: Perpendicular(g160,g159)
    c: PointOnObject(g163,g159)
    c: Distance(g163,g159) = 1.1
    c: Distance(g159,g159) = 2.2
    c: Distance(g159,g160) = 1.5
    c: Coincident(g163,g165)
    c: Perpendicular(g165,g159)
    c: Angle(g165,g164) = 0.15708
    c: Angle(g166,g165) = 0.15708
    c: Angle(g164,g133) = 0.15708
    c: Equal(g133,g164)
    c: Equal(g164,g165)
    c: Equal(g165,g166)
    c: Coincident(g167,g153)
    c: Perpendicular(g167,g149)
    c: Equal(g166,g167)
    c: Angle(g167,g132) = -0.15708
    c: Equal(g132,g167)
    c: Coincident(g168,g138)
    c: Equal(g133,g168)
    c: Perpendicular(g168,g134)
    c: Coincident(g170,g169)
    c: Coincident(g171,g170)
    c: Coincident(g172,g171)
    c: Coincident(g172,g169)
    c: Equal(g169,g171)
    c: Parallel(g170,g172)
    c: Perpendicular(g170,g169)
    c: PointOnObject(g173,g169)
    c: Distance(g173,g169) = 1.1
    c: Distance(g169,g169) = 2.2
    c: Distance(g169,g170) = 1.5
    c: Coincident(g173,g229)
    c: Perpendicular(g229,g169)
    c: Angle(g230,g229) = 0.15708
    c: Coincident(g175,g174)
    c: Coincident(g176,g175)
    c: Coincident(g177,g176)
    c: Coincident(g177,g174)
    c: Equal(g174,g176)
    c: Parallel(g175,g177)
    c: Perpendicular(g175,g174)
    c: PointOnObject(g178,g174)
    c: Distance(g178,g174) = 1.1
    c: Equal(g169,g174) = 2.2
    c: Distance(g174,g175) = 1.5
    c: Coincident(g178,g230)
    c: Perpendicular(g230,g174)
    c: Distance(g169,g174) = 2.22
    c: Coincident(g180,g179)
    c: Coincident(g181,g180)
    c: Coincident(g182,g181)
    c: Coincident(g182,g179)
    c: Equal(g179,g181)
    c: Parallel(g180,g182)
    c: Perpendicular(g180,g179)
    c: PointOnObject(g183,g179)
    c: Distance(g183,g179) = 1.1
    c: Distance(g179,g179) = 2.2
    c: Distance(g179,g180) = 1.5
    c: Coincident(g183,g231)
    c: Perpendicular(g231,g179)
    c: Coincident(g185,g184)
    c: Coincident(g186,g185)
    c: Coincident(g187,g186)
    c: Coincident(g187,g184)
    c: Equal(g184,g186)
    c: Parallel(g185,g187)
    c: Perpendicular(g185,g184)
    c: PointOnObject(g188,g184)
    c: Distance(g188,g184) = 1.1
    c: Distance(g184,g184) = 2.2
    c: Distance(g184,g185) = 1.5
    c: Coincident(g190,g189)
    c: Coincident(g191,g190)
    c: Coincident(g192,g191)
    c: Coincident(g192,g189)
    c: Equal(g189,g191)
    c: Parallel(g190,g192)
    c: Perpendicular(g190,g189)
    c: PointOnObject(g193,g189)
    c: Distance(g193,g189) = 1.1
    c: Equal(g184,g189) = 2.2
    c: Distance(g189,g190) = 1.5
    c: Coincident(g193,g232)
    c: Perpendicular(g232,g189)
    c: Distance(g184,g189) = 2.22
    c: Coincident(g195,g194)
    c: Coincident(g196,g195)
    c: Coincident(g197,g196)
    c: Coincident(g197,g194)
    c: Equal(g194,g196)
    c: Parallel(g195,g197)
    c: Perpendicular(g195,g194)
    c: PointOnObject(g198,g194)
    c: Distance(g198,g194) = 1.1
    c: Distance(g194,g194) = 2.2
    c: Distance(g194,g195) = 1.5
    c: Coincident(g198,g233)
    c: Perpendicular(g233,g194)
    c: Angle(g233,g231) = 0.15708
    c: Angle(g232,g233) = 0.15708
    c: Angle(g231,g230) = 0.15708
    c: Equal(g230,g231)
    c: Equal(g231,g233)
    c: Equal(g233,g232)
    c: Coincident(g234,g188)
    c: Perpendicular(g234,g184)
    c: Equal(g232,g234)
    c: Coincident(g200,g199)
    c: Coincident(g201,g200)
    c: Coincident(g202,g201)
    c: Coincident(g202,g199)
    c: Equal(g199,g201)
    c: Parallel(g200,g202)
    c: Perpendicular(g200,g199)
    c: PointOnObject(g203,g199)
    c: Distance(g203,g199) = 1.1
    c: Distance(g199,g199) = 2.2
    c: Distance(g199,g200) = 1.5
    c: Coincident(g205,g204)
    c: Coincident(g206,g205)
    c: Coincident(g207,g206)
    c: Coincident(g207,g204)
    c: Equal(g204,g206)
    c: Parallel(g205,g207)
    c: Perpendicular(g205,g204)
    c: PointOnObject(g208,g204)
    c: Distance(g208,g204) = 1.1
    c: Equal(g199,g204) = 2.2
    c: Distance(g204,g205) = 1.5
    c: Coincident(g208,g238)
    c: Perpendicular(g238,g204)
    c: Distance(g199,g204) = 2.22
    c: Coincident(g210,g209)
    c: Coincident(g211,g210)
    c: Coincident(g212,g211)
    c: Coincident(g212,g209)
    c: Equal(g209,g211)
    c: Parallel(g210,g212)
    c: Perpendicular(g210,g209)
    c: PointOnObject(g213,g209)
    c: Distance(g213,g209) = 1.1
    c: Distance(g209,g209) = 2.2
    c: Distance(g209,g210) = 1.5
    c: Coincident(g213,g239)
    c: Perpendicular(g239,g209)
    c: Coincident(g215,g214)
    c: Coincident(g216,g215)
    c: Coincident(g217,g216)
    c: Coincident(g217,g214)
    c: Equal(g214,g216)
    c: Parallel(g215,g217)
    c: Perpendicular(g215,g214)
    c: PointOnObject(g218,g214)
    c: Distance(g218,g214) = 1.1
    c: Distance(g214,g214) = 2.2
    c: Distance(g214,g215) = 1.5
    c: Coincident(g220,g219)
    c: Coincident(g221,g220)
    c: Coincident(g222,g221)
    c: Coincident(g222,g219)
    c: Equal(g219,g221)
    c: Parallel(g220,g222)
    c: Perpendicular(g220,g219)
    c: PointOnObject(g223,g219)
    c: Distance(g223,g219) = 1.1
    c: Equal(g214,g219) = 2.2
    c: Distance(g219,g220) = 1.5
    c: Coincident(g223,g236)
    c: Perpendicular(g236,g219)
    c: Distance(g214,g219) = 2.22
    c: Coincident(g225,g224)
    c: Coincident(g226,g225)
    c: Coincident(g227,g226)
    c: Coincident(g227,g224)
    c: Equal(g224,g226)
    c: Parallel(g225,g227)
    c: Perpendicular(g225,g224)
    c: PointOnObject(g228,g224)
    c: Distance(g228,g224) = 1.1
    c: Distance(g224,g224) = 2.2
    c: Distance(g224,g225) = 1.5
    c: Coincident(g228,g235)
    c: Perpendicular(g235,g224)
    c: Angle(g235,g239) = -0.15708
    c: Angle(g236,g235) = -0.15708
    c: Angle(g239,g238) = -0.15708
    c: Equal(g238,g239)
    c: Equal(g239,g235)
    c: Equal(g235,g236)
    c: Coincident(g237,g218)
    c: Perpendicular(g237,g214)
    c: Equal(g236,g237)
    c: Angle(g237,g234) = 0.15708
    c: Equal(g234,g237)
    c: Coincident(g240,g203)
    c: Equal(g238,g240)
    c: Perpendicular(g240,g199)
    c: Angle(g240,g168) = -0.15708
    c: Coincident(g234,g239)
    c: Coincident(g234,g235)
    c: Coincident(g234,g236)
    c: Equal(g168,g240)
    c: Equal(g229,g230)
    c: Angle(g229,g109) = 0.15708
    c: Coincident(g231,g237)
    c: Coincident(g231,g232)
    c: Coincident(g231,g229)
    c: Coincident(g231,g230)
    c: Coincident(g231,g233)
    c: Coincident(g231,g167)
    c: Coincident(g231,g133)
    c: Coincident(g231,g168)
    c: Coincident(g231,g164)
    c: Coincident(g231,g0)
    c: Coincident(g131,g0)
    c: Coincident(g238,g0)
    c: Coincident(g166,g0)
    c: Coincident(g132,g0)
    c: Coincident(g240,g234)
    c: Coincident(g240,g0)
    c: Coincident(g165,g0)
    c: Coincident(g241,g104)
    c: Coincident(g241,g99)
    c: Tangent(g241,g0)
    c: Coincident(g242,g102)
    c: Coincident(g242,g94)
    c: Tangent(g242,g0)
    c: Coincident(g243,g97)
    c: Coincident(g243,g64)
    c: Coincident(g244,g65)
    c: Coincident(g244,g72)
    c: Coincident(g245,g70)
    c: Coincident(g246,g77)
    c: Coincident(g245,g75)
    c: Coincident(g246,g62)
    c: Coincident(g247,g60)
    c: Coincident(g248,g57)
    c: Coincident(g247,g55)
    c: Coincident(g248,g50)
    c: Coincident(g249,g52)
    c: Coincident(g250,g170)
    c: Coincident(g249,g172)
    c: Coincident(g250,g174)
    c: Coincident(g251,g175)
    c: Coincident(g252,g182)
    c: Coincident(g251,g180)
    c: Coincident(g252,g194)
    c: Coincident(g253,g195)
    c: Coincident(g253,g190)
    c: Coincident(g254,g192)
    c: Coincident(g255,g187)
    c: Coincident(g185,g254)
    c: Coincident(g214,g255)
    c: Coincident(g256,g215)
    c: Coincident(g257,g220)
    c: Coincident(g256,g222)
    c: Coincident(g257,g225)
    c: Coincident(g258,g227)
    c: Coincident(g258,g209)
    c: Coincident(g259,g210)
    c: Coincident(g260,g207)
    c: Coincident(g205,g259)
    c: Coincident(g199,g260)
    c: Coincident(g261,g202)
    c: Coincident(g262,g135)
    c: Coincident(g263,g140)
    c: Coincident(g137,g261)
    c: Coincident(g142,g262)
    c: Coincident(g263,g144)
    c: Coincident(g264,g147)
    c: Coincident(g265,g160)
    c: Coincident(g264,g162)
    c: Coincident(g265,g154)
    c: Coincident(g266,g157)
    c: Coincident(g266,g150)
    c: Coincident(g267,g152)
    c: Coincident(g268,g122)
    c: Coincident(g267,g124)
    c: Coincident(g268,g129)
    c: Coincident(g269,g127)
    c: Coincident(g270,g9)
    c: Coincident(g269,g7)
    c: Coincident(g270,g2)
    c: Coincident(g271,g4)
    c: Coincident(g272,g29)
    c: Coincident(g271,g29)
    c: Coincident(g272,g34)
    c: Coincident(g273,g35)
    c: Coincident(g274,g42)
    c: Coincident(g273,g40)
    c: Coincident(g274,g24)
    c: Coincident(g275,g22)
    c: Coincident(g276,g14)
    c: Coincident(g277,g79)
    c: Coincident(g278,g84)
    c: Coincident(g279,g89)
    c: Coincident(g279,g107)
    c: Coincident(g278,g89)
    c: Coincident(g277,g84)
    c: Coincident(g276,g79)
    c: Coincident(g275,g14)
    c: Coincident(g280,g25)
    c: Coincident(g280,g20)
FEATURE [PartDesign::Pad] Pad
  Direction = (1,1,1)
  Length = 9
  Length2 = 100
  Profile = -> Sketch
  Type = 0
FEATURE [PartDesign::Body] Body
  Group = -> [Sketch,Pad]
  Origin = -> Origin
  Tip = -> Pad
